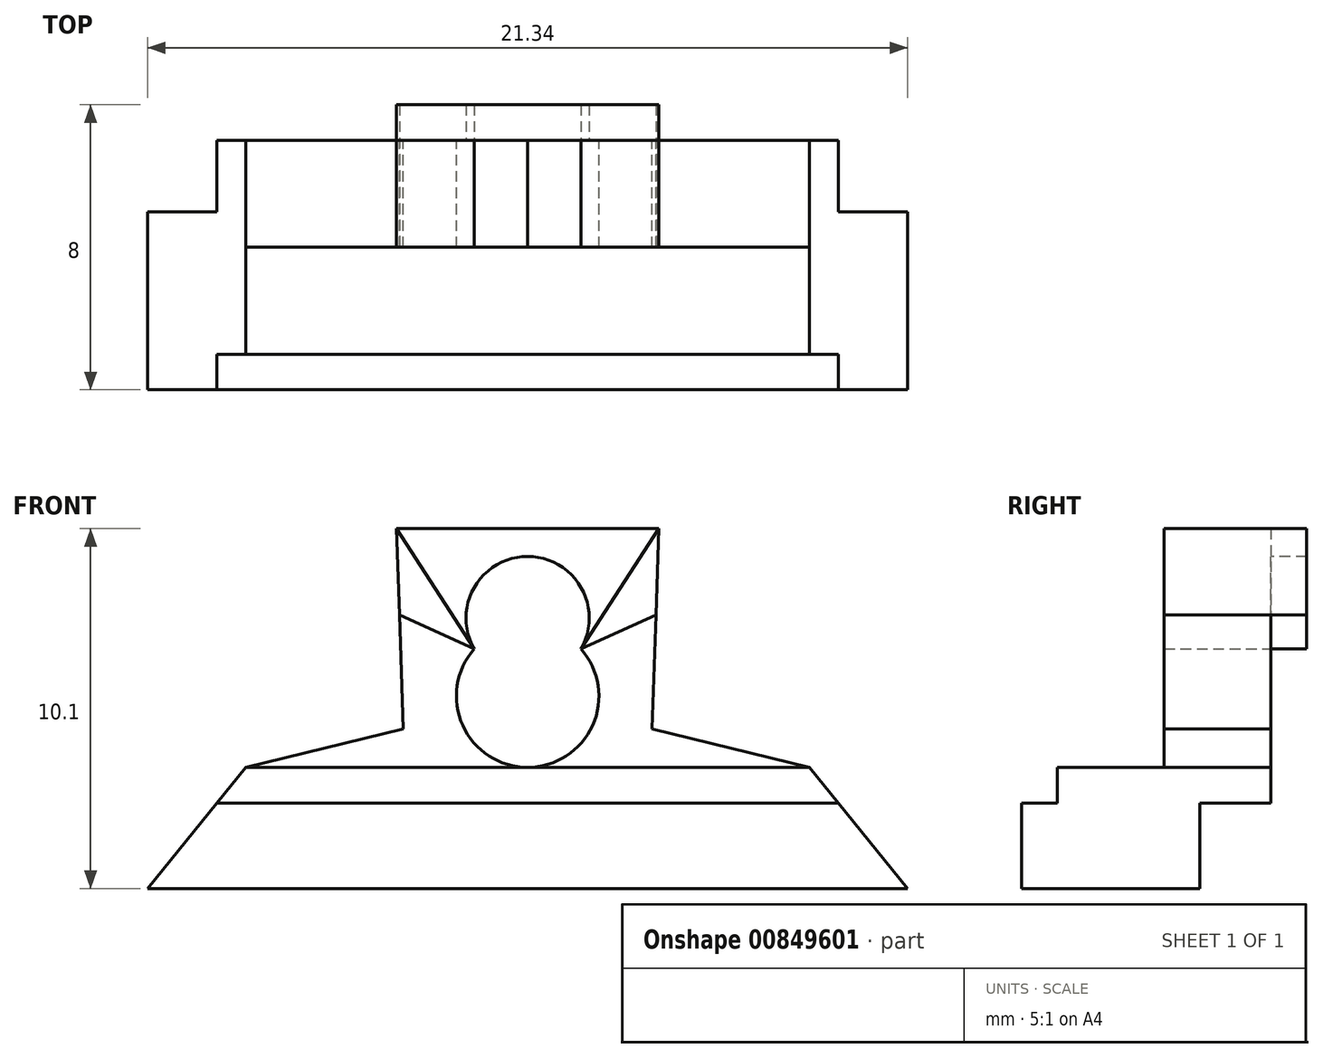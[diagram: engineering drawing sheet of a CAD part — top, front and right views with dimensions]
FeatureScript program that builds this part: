
annotation { "Feature Type Name" : "Feature", "Feature Type Description" : "" }
export const myFeature = defineFeature(function(context is Context, id is Id, definition is map)
    precondition{}
    {
        {
            var Q0;
            Q0=qCreatedBy(makeId("Front.planeOp"),FACE);
            var sketch = newSketch(context, id + "F0", { "sketchPlane" : qUnion([Q0])});
            skLineSegment(sketch, "E0", {"start": v(3.68, 6.7) * mm, "end": v(1.5, 3.32) * mm});
            skLineSegment(sketch, "E1.MirrorCS", {"start": v(7.9, 0) * mm, "end": v(3.5, 1.08) * mm});
            skLineSegment(sketch, "E2", {"start": v(3.68, 6.7) * mm, "end": v(3.5, 1.08) * mm});
            skLineSegment(sketch, "E3.MirrorCS", {"start": v(-3.68, 6.7) * mm, "end": v(-1.5, 3.32) * mm});
            skLineSegment(sketch, "E4.MirrorCS", {"start": v(-3.68, 6.7) * mm, "end": v(-3.5, 1.08) * mm});
            skLineSegment(sketch, "E5.MirrorCS", {"start": v(-7.9, 0) * mm, "end": v(-3.5, 1.08) * mm});
            skLineSegment(sketch, "E6", {"start": v(-7.9, 0) * mm, "end": v(7.9, 0) * mm});
            skLineSegment(sketch, "E7", {"start": v(7.9, 0) * mm, "end": v(10.67, -3.4) * mm});
            skLineSegment(sketch, "E8", {"start": v(10.67, -3.4) * mm, "end": v(0, -3.4) * mm});
            skLineSegment(sketch, "E9.MirrorCS", {"start": v(-7.9, 0) * mm, "end": v(-10.67, -3.4) * mm});
            skLineSegment(sketch, "E10.MirrorCS", {"start": v(-10.67, -3.4) * mm, "end": v(0, -3.4) * mm});
            skArc(sketch, "E11", {"start": v(-1.5, 3.32) * mm, "mid": v(0, 0) * mm, "end": v(1.5, 3.32) * mm});
            skLineSegment(sketch, "E12", {"start": v(-8.72, -1) * mm, "end": v(8.72, -1) * mm});
            skLineSegment(sketch, "E13", {"start": v(1.5, 3.32) * mm, "end": v(3.6, 4.28) * mm});
            skLineSegment(sketch, "E14", {"start": v(1.5, 3.32) * mm, "end": v(0, 3.32) * mm});
            skLineSegment(sketch, "E15", {"start": v(3.68, 6.7) * mm, "end": v(0, 6.7) * mm});
            skLineSegment(sketch, "E16.MirrorCS", {"start": v(-3.68, 6.7) * mm, "end": v(0, 6.7) * mm});
            skLineSegment(sketch, "E17.MirrorCS", {"start": v(-1.5, 3.32) * mm, "end": v(-3.6, 4.28) * mm});
            skLineSegment(sketch, "E18.MirrorCS", {"start": v(-1.5, 3.32) * mm, "end": v(0, 3.32) * mm});
            skArc(sketch, "E19", {"start": v(1.5, 3.32) * mm, "mid": v(0, 5.92) * mm, "end": v(-1.5, 3.32) * mm});
            skSolve(sketch);
        }
        {
            var Q0;
            Q0=makeQuery(id+"F0.imprint","IMPRINT",FACE,{"disambiguationData":[TD([[makeQuery(id+"F0.imprint","IMPRINT",EDGE,{"derivedFrom":sQuery(id+"F0.wireOp",EDGE,"E6")}),-1.0]])]});
            extrude(context, id + "F1", {"entities" : qUnion([Q0]), "depth" : 4 * mm, "offsetDistance" : 25.4 * mm, "hasSecondDirection" : true, "secondDirectionOppositeDirection" : true, "secondDirectionDepth" : 2 * mm});
        }
        {
            var Q0;
            {var subQ4=sQuery(id+"F0.wireOp",EDGE,"E0");Q0=makeQuery(id+"F0.imprint","IMPRINT",FACE,{"disambiguationData":[TD([[makeQuery(id+"F0.imprint","IMPRINT",EDGE,{"derivedFrom":subQ4}),1.0]])]});}
            var Q1;
            {var subQ4=sQuery(id+"F0.wireOp",EDGE,"E3.MirrorCS");Q1=makeQuery(id+"F0.imprint","IMPRINT",FACE,{"disambiguationData":[TD([[makeQuery(id+"F0.imprint","IMPRINT",EDGE,{"derivedFrom":subQ4}),-1.0]])]});}
            var Q2;
            Q2=makeQuery(id+"F0.imprint","IMPRINT",FACE,{"disambiguationData":[TD([[makeQuery(id+"F0.imprint","IMPRINT",EDGE,{"derivedFrom":sQuery(id+"F0.wireOp",EDGE,"E0")}),-1.0]])]});
            extrude(context, id + "F2", {"entities" : qUnion([Q0, Q1, Q2]), "operationType" : NewBodyOperationType.ADD, "oppositeDirection" : true, "depth" : 3 * mm, "offsetDistance" : 25.4 * mm, "hasSecondDirection" : true, "secondDirectionOppositeDirection" : false, "secondDirectionDepth" : 1 * mm});
        }
        {
            var Q0;
            {var subQ3=sQuery(id+"F0.wireOp",EDGE,"E8");Q0=makeQuery(id+"F0.imprint","IMPRINT",FACE,{"disambiguationData":[TD([[makeQuery(id+"F0.imprint","IMPRINT",EDGE,{"derivedFrom":subQ3}),-1.0]])]});}
            extrude(context, id + "F3", {"entities" : qUnion([Q0]), "operationType" : NewBodyOperationType.ADD, "depth" : 5 * mm, "offsetDistance" : 25.4 * mm});
        }
        {
            var Q0;
            {var subQ1=sQuery(id+"F0.wireOp",EDGE,"E5.MirrorCS");Q0=makeQuery(id+"F0.imprint","IMPRINT",FACE,{"disambiguationData":[TD([[makeQuery(id+"F0.imprint","IMPRINT",EDGE,{"derivedFrom":subQ1}),-1.0]])]});}
            var Q1;
            {var subQ4=sQuery(id+"F0.wireOp",EDGE,"E1.MirrorCS");Q1=makeQuery(id+"F0.imprint","IMPRINT",FACE,{"disambiguationData":[TD([[makeQuery(id+"F0.imprint","IMPRINT",EDGE,{"derivedFrom":subQ4}),1.0]])]});}
            extrude(context, id + "F4", {"entities" : qUnion([Q0, Q1]), "depth" : 1 * mm, "offsetDistance" : 25 * mm, "hasSecondDirection" : true, "secondDirectionOppositeDirection" : true, "secondDirectionDepth" : 2 * mm});
        }
        {
            var Q0;
            Q0=makeQuery(id+"F0.imprint","IMPRINT",FACE,{"disambiguationData":[TD([[makeQuery(id+"F0.imprint","IMPRINT",EDGE,{"derivedFrom":sQuery(id+"F0.wireOp",EDGE,"E0")}),-1.0]])]});
            extrude(context, id + "F5", {"entities" : qUnion([Q0]), "operationType" : NewBodyOperationType.REMOVE, "oppositeDirection" : true, "depth" : 2 * mm, "offsetDistance" : 25 * mm, "hasSecondDirection" : true, "secondDirectionOppositeDirection" : false, "secondDirectionDepth" : 2 * mm});
        }
    });
